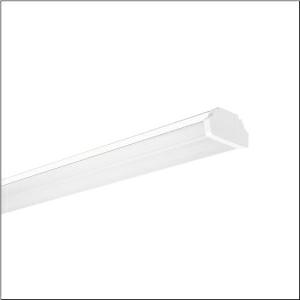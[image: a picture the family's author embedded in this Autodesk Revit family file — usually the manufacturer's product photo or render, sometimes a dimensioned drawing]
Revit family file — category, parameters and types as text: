
# Revit family: dus_r__31_ho_53bd812d2v4120_dd06
name_source: partatom
category: Lighting Fixtures
units: mm (PartAtom-declared; Revit-internal decimal feet)

## family parameters
Cut with Voids When Loaded = No
Host = Face
Light Source = No
Part Type = Normal
Room Calculation Point = No
Round Connector Dimension = Use Diameter
Shared = No

## types (1)
- --- (1 x LED, 12350 lm, 79.5 W, 4000K)
    Apparent Load = 80 VA
    CIE Flux Codes = 47 80 95 92 100
    Color Rendering = 80
    Color Temperature = 4000K
    Default Elevation = 1800 mm
    Description = DUS® 31 HO, luminaire insert, of sheet steel, coil coated, white, length: 1.535mm, width: 81mm, height: 90mm, 5x system unit, system units: 307mm, LED rated luminous flux: 12.350lm, light colour: 840, control gear: DALI 2, control gear: ECG DALI, with plug, 5-pole, with phase selection, mains connection: 220..240V, AC, 50/60Hz, rated input power: 80W, through-wiring accessed according to module size, primary optical cover: cover, of PMMA, light emission: direct distribution, primary light characteristic: symmetric, protection rating (complete): IP20, protection rating (LED compartment): IP50, insulation class (complete): insulation class I (protective earthing), certification: CE, ENEC, VDE, UKCA, impact resistance: IK03, permissible ambient temperature for indoor applications: -25..+30°C, corresponds to IFS (International Featured Standards) requirements for safety and quality in the food industry, reducing of maximum allowable ambient temperature of 5°C with ceiling mounting, packaging unit: 1 piece
    Height = 95 mm
    Lamp = 1 x LED
    Lamp Light Flux = 12350 lm
    Lamp Power = 79.5 W
    Lamp count = 1
    Length = 1535 mm
    Luminous efficacy = 155 lm/W
    Manufacturer = Siteco
    ModVariant = No
    Model = 53BD812D2V4120
    Mounting Place = Ceiling
    Mounting Type = Pendant
    Number of Poles = 1
    OnlyDefault = Yes
    Power Factor = 1
    Product Name = DUS® 31 HO
    Product group = luminaire insert
    ProductGroupID = 901
    Protection Class = Protection class I
    Protection Degree = IP 20
    RLX_Detail_Level = 1
    RLX_Emergency_Light_Flux = 0 lm
    RLX_Emergency_Type = 0
    RLX_Emergency_Type_DB = No
    RlxData = <blob elided: 42209 chars, md5=0dbb6b82>
    Socket = socket
    Standby Power = 0 W
    System Light Flux = 12350 lm
    System Power = 80 W
    Type Comments = factory setting: luminous flux: 100 % | dim-lin: 254 | 345 mA
    Type Image = l_1003451.jpg
    URL = http://relux.com
    VarID = @adj_140145
    Voltage = 0 V
    Weight = 0.00 kg
    Width = 81 mm

## geometry (parser evidence)
native form markers: Blend x4, Sweep x11
no freeform markers — native parametric forms only
